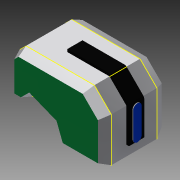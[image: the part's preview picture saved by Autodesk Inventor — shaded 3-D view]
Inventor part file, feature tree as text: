
AUTODESK INVENTOR PART (.ipt)
format: ipt  version: 2014 (Build 180170000, 170)  size: 269,824 bytes
history: native  units: in
note: dims shown in document units (in); Inventor stores cm internally (conversion verified against a paired STEP export)
features: sketch x11, extrude x7, other x3, plane x2, loft x2
ambient origin geometry x8: Origin, YZ Plane, XZ Plane, XY Plane, X Axis, Y Axis, Z Axis, Center Point
bodies: Solid1 (feature_tree)
feature tree (25):
  extrude  "Extrusion1"  Depth=1.08in
  sketch  "Sketch2"  dims[d27=1.08in d33=0.0in d34=90.0deg]
  sketch  "Sketch3"  dims[d35=0.0in d36=90.0deg d38=7.56in d39=0.0in]
  plane  "Work Plane1"
  plane  "Work Plane2"
  loft  "Loft1"
  extrude  "Extrusion2"  Depth=7.56in TaperAngle=0.0deg
  loft  "Loft2"
  extrude  "Extrusion3"  Depth=1.8in
  extrude  "Extrusion4"  Depth=1.8in
  extrude  "Extrusion5"  Depth=0.3in TaperAngle=0.0deg
  sketch  "Sketch9"  dims[d55=0.3in d56=0.3in]
  extrude  "Extrusion6"  Depth=0.3in TaperAngle=0.0deg
  extrude  "Extrusion7"  Depth=0.3in
  sketch  "Sketch1"  dims[d24=5.4in d25=0.0in d26=1.08in]
  sketch  "Sketch4"  dims[d40=0.0in d41=90.0deg d42=0.0in d43=90.0deg]
  other  "Edges1"
  sketch  "Sketch5"  dims[d44=1.8in d45=1.8in]
  other  "Edges2"
  other  "Edges3"
  sketch  "Sketch6"  dims[d46=0.3in d47=0.0in d48=1.8in]
  sketch  "Sketch7"  dims[d49=5.0in d50=0.3in d51=0.0in]
  sketch  "Sketch8"  dims[d52=4.0in d53=0.3in d54=0.0in]
  sketch  "Sketch10"  dims[d57=45.0deg]
  sketch  "Sketch11"  dims[d58=1.8in d59=0.0in d60=1.0in d61=0.1in d62=0.0in]
